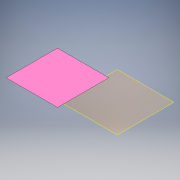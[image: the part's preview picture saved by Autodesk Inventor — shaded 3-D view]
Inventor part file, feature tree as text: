
AUTODESK INVENTOR PART (.ipt)
format: ipt  version: 2018.3 (Build 223284000, 284)  size: 125,440 bytes
history: native  units: mm
features: extrude x2, sketch x2, plane x1, chamfer x1
ambient origin geometry x8: Origin, YZ Plane, XZ Plane, XY Plane, X Axis, Y Axis, Z Axis, Center Point
bodies: Body1 (feature_tree)
feature tree (6):
  plane  "Arbeitsebene1"
  extrude  "Extrusion2"  Depth=18.0mm
  chamfer  "Fase2"  Distance=18.0mm
  extrude  "Extrusion3"  Depth=55.0mm
  sketch  "Skizze2"  dims[d5=440.0mm d6=440.0mm d7=18.0mm d8=0.0mm]
  sketch  "Skizze3"  dims[d9=18.0mm d10=2.0mm d11=45.0deg d12=55.0mm d13=110.0mm d14=20.0mm d15=20.0mm d16=4.0mm d17=15.0mm d18=0.0mm]
